# Revit family: Lüftungsrohrschelle , M 8, Gummi
name_source: partatom
category: HLS-Bauteile
revit_build: Autodesk Revit 2017 (Build: 20190507_1515(x64)
units: mm (PartAtom-declared; Revit-internal decimal feet)

## family parameters
Arbeitsebenenbasiert = Ja
Beim Laden mit Abzugskörper schneiden = Nein
Bemaßung runder Anschluss = Durchmesser verwenden
Gemeinsam genutzt = Ja
Immer vertikal = Nein
Raumberechnungspunkt = Nein
Teiletyp = Normal

## types (21) — shared parameters
Anschluss = M8
Bauart = zweiteilig
Baustoffklasse = B2
DF1 = 25 mm  [stored 0.082021 ft]
DS = 6 mm  [stored 0.019685 ft]
DVS = 8 mm  [stored 0.0262467 ft]
Dämmstärke = 6 mm  [stored 0.019685 ft]
Fabrikat = MEFA
Farbe Schalldämmeinlage = schwarz
Firma = MEFA Befestigungs- und Montagesysteme GmbH
Material = Stahl
Material Schalldämmeinlage = TPE
Materialname = S235
Mengeneinheit = St
Oberflaeche = galvanisch verzinkt
Rohraußendurchmesser Zoll = Zoll
Schalldämmeinlage = Gummi
Verschluss = Mutter / Verschluss-Schraube
Verschluss-Schraube = M8
Vorgabe-Ansicht = 1219 mm
max. Temperaturbeständigkeit = 100 °C
max. zul. Last horizontal = 0.00 kN
max. zul. Last vertikal = 0.00 kN
vpe = 1 St
zero-valued in all types: AB, Stärke Material, max. Rohraußendurchmesser, min. Rohraußendurchmesser

## per-type parameters (varying)
- Lüftungsrohrschelle, M 8, DN  71, Gummi: A=22 mm  [stored 0.0721785 ft]; Achsabstand=120 mm; Anschlußhöhe=22 mm; Artikelnummer=0430711; B=145 mm; Breite=145 mm; D=73 mm  [stored 0.239501 ft]; D0=85 mm  [stored 0.278871 ft]; DF2=35 mm  [stored 0.114829 ft]; EAN=4250928409355; Gewicht=0.21 kg; Gewicht pro Bauteil=0.21 kg; H=103 mm; HGA=14 mm  [stored 0.0459318 ft]; Höhe=103 mm; Kurztext1=Lüftungsschelle Standard 20x2,0; Kurztext2=DN 71 M8 TPE; MB=20 mm  [stored 0.0656168 ft]; MD=2 mm  [stored 0.00656168 ft]; Materialmaße=20x2,0 mm; Nennweite DN Rohr=71 mm  [stored 0.23294 ft]; R=43 mm; RM=45 mm; Rohraußendurchmesser=73 mm  [stored 0.239501 ft]; S=120 mm; max. Höhe=103 mm; max. zul. Last=0.80 kN
- Lüftungsrohrschelle, M 8, DN  80, Gummi: A=22 mm  [stored 0.0721785 ft]; Achsabstand=129 mm; Anschlußhöhe=22 mm; Artikelnummer=0430801; B=154 mm; Breite=154 mm; D=82 mm  [stored 0.269029 ft]; D0=94 mm  [stored 0.308399 ft]; DF2=35 mm  [stored 0.114829 ft]; EAN=4250928409409; Gewicht=0.22 kg; Gewicht pro Bauteil=0.22 kg; H=112 mm; HGA=14 mm  [stored 0.0459318 ft]; Höhe=112 mm; Kurztext1=Lüftungsschelle Standard 20x2,0; Kurztext2=DN 80 M8 TPE; MB=20 mm  [stored 0.0656168 ft]; MD=2 mm  [stored 0.00656168 ft]; Materialmaße=20x2,0 mm; Nennweite DN Rohr=80 mm  [stored 0.262467 ft]; R=47 mm  [stored 0.154199 ft]; RM=49 mm  [stored 0.160761 ft]; Rohraußendurchmesser=82 mm  [stored 0.269029 ft]; S=129 mm; max. Höhe=112 mm; max. zul. Last=0.80 kN
- Lüftungsrohrschelle, M 8, DN  90, Gummi: A=22 mm  [stored 0.0721785 ft]; Achsabstand=139 mm; Anschlußhöhe=22 mm; Artikelnummer=0430901; B=164 mm; Breite=164 mm; D=92 mm  [stored 0.301837 ft]; D0=104 mm; DF2=35 mm  [stored 0.114829 ft]; EAN=4250928409454; Gewicht=0.23 kg; Gewicht pro Bauteil=0.23 kg; H=122 mm; HGA=14 mm  [stored 0.0459318 ft]; Höhe=122 mm; Kurztext1=Lüftungsschelle Standard 20x2,0; Kurztext2=DN 90 M8 TPE; MB=20 mm  [stored 0.0656168 ft]; MD=2 mm  [stored 0.00656168 ft]; Materialmaße=20x2,0 mm; Nennweite DN Rohr=90 mm  [stored 0.295276 ft]; R=52 mm  [stored 0.170604 ft]; RM=54 mm  [stored 0.177165 ft]; Rohraußendurchmesser=92 mm  [stored 0.301837 ft]; S=139 mm; max. Höhe=122 mm; max. zul. Last=0.80 kN
- Lüftungsrohrschelle, M 8, DN 100, Gummi: A=22 mm  [stored 0.0721785 ft]; Achsabstand=150 mm; Anschlußhöhe=22 mm; Artikelnummer=0431001; B=175 mm; Breite=175 mm; D=103 mm; D0=115 mm; DF2=35 mm  [stored 0.114829 ft]; EAN=4250928409508; Gewicht=0.25 kg; Gewicht pro Bauteil=0.25 kg; H=133 mm; HGA=14 mm  [stored 0.0459318 ft]; Höhe=133 mm; Kurztext1=Lüftungsschelle Standard 20x2,0; Kurztext2=DN 100 M8 TPE; MB=20 mm  [stored 0.0656168 ft]; MD=2 mm  [stored 0.00656168 ft]; Materialmaße=20x2,0 mm; Nennweite DN Rohr=100 mm; R=58 mm  [stored 0.190289 ft]; RM=60 mm; Rohraußendurchmesser=103 mm; S=150 mm; max. Höhe=133 mm; max. zul. Last=0.80 kN
- Lüftungsrohrschelle, M 8, DN 112, Gummi: A=22 mm  [stored 0.0721785 ft]; Achsabstand=162 mm; Anschlußhöhe=22 mm; Artikelnummer=0431121; B=187 mm; Breite=187 mm; D=115 mm; D0=127 mm; DF2=35 mm  [stored 0.114829 ft]; EAN=4250928409553; Gewicht=0.26 kg; Gewicht pro Bauteil=0.26 kg; H=145 mm; HGA=14 mm  [stored 0.0459318 ft]; Höhe=145 mm; Kurztext1=Lüftungsschelle Standard 20x2,0; Kurztext2=DN 112 M8 TPE; MB=20 mm  [stored 0.0656168 ft]; MD=2 mm  [stored 0.00656168 ft]; Materialmaße=20x2,0 mm; Nennweite DN Rohr=112 mm; R=64 mm; RM=66 mm; Rohraußendurchmesser=115 mm; S=162 mm; max. Höhe=145 mm; max. zul. Last=0.80 kN
- Lüftungsrohrschelle, M 8, DN 125, Gummi: A=22 mm  [stored 0.0721785 ft]; Achsabstand=175 mm; Anschlußhöhe=22 mm; Artikelnummer=0431251; B=200 mm; Breite=200 mm; D=128 mm; D0=140 mm; DF2=35 mm  [stored 0.114829 ft]; EAN=4250928409607; Gewicht=0.28 kg; Gewicht pro Bauteil=0.28 kg; H=158 mm; HGA=14 mm  [stored 0.0459318 ft]; Höhe=158 mm; Kurztext1=Lüftungsschelle Standard 20x2,0; Kurztext2=DN 125 M8 TPE; MB=20 mm  [stored 0.0656168 ft]; MD=2 mm  [stored 0.00656168 ft]; Materialmaße=20x2,0 mm; Nennweite DN Rohr=125 mm; R=70 mm  [stored 0.229659 ft]; RM=72 mm  [stored 0.23622 ft]; Rohraußendurchmesser=128 mm; S=175 mm; max. Höhe=158 mm; max. zul. Last=0.80 kN
- Lüftungsrohrschelle, M 8, DN 140, Gummi: A=22 mm  [stored 0.0721785 ft]; Achsabstand=190 mm; Anschlußhöhe=22 mm; Artikelnummer=0431401; B=215 mm; Breite=215 mm; D=143 mm; D0=155 mm; DF2=35 mm  [stored 0.114829 ft]; EAN=4250928409652; Gewicht=0.30 kg; Gewicht pro Bauteil=0.30 kg; H=173 mm; HGA=14 mm  [stored 0.0459318 ft]; Höhe=173 mm; Kurztext1=Lüftungsschelle Standard 20x2,0; Kurztext2=DN 140 M8 TPE; MB=20 mm  [stored 0.0656168 ft]; MD=2 mm  [stored 0.00656168 ft]; Materialmaße=20x2,0 mm; Nennweite DN Rohr=140 mm; R=78 mm; RM=80 mm  [stored 0.262467 ft]; Rohraußendurchmesser=143 mm; S=190 mm; max. Höhe=173 mm; max. zul. Last=0.80 kN
- Lüftungsrohrschelle, M 8, DN 150, Gummi: A=22 mm  [stored 0.0721785 ft]; Achsabstand=200 mm; Anschlußhöhe=22 mm; Artikelnummer=0431501; B=225 mm; Breite=225 mm; D=153 mm; D0=165 mm; DF2=35 mm  [stored 0.114829 ft]; EAN=4250928409706; Gewicht=0.32 kg; Gewicht pro Bauteil=0.32 kg; H=183 mm; HGA=14 mm  [stored 0.0459318 ft]; Höhe=183 mm; Kurztext1=Lüftungsschelle Standard 20x2,0; Kurztext2=DN 150 M8 TPE; MB=20 mm  [stored 0.0656168 ft]; MD=2 mm  [stored 0.00656168 ft]; Materialmaße=20x2,0 mm; Nennweite DN Rohr=150 mm; R=83 mm; RM=85 mm  [stored 0.278871 ft]; Rohraußendurchmesser=153 mm; S=200 mm; max. Höhe=183 mm; max. zul. Last=0.80 kN
- Lüftungsrohrschelle, M 8, DN 160, Gummi: A=22 mm  [stored 0.0721785 ft]; Achsabstand=210 mm; Anschlußhöhe=22 mm; Artikelnummer=0431601; B=235 mm; Breite=235 mm; D=163 mm; D0=175 mm; DF2=35 mm  [stored 0.114829 ft]; EAN=4250928409751; Gewicht=0.33 kg; Gewicht pro Bauteil=0.33 kg; H=193 mm; HGA=14 mm  [stored 0.0459318 ft]; Höhe=193 mm; Kurztext1=Lüftungsschelle Standard 20x2,0; Kurztext2=DN 160 M8 TPE; MB=20 mm  [stored 0.0656168 ft]; MD=2 mm  [stored 0.00656168 ft]; Materialmaße=20x2,0 mm; Nennweite DN Rohr=160 mm; R=88 mm; RM=90 mm  [stored 0.295276 ft]; Rohraußendurchmesser=163 mm; S=210 mm; max. Höhe=193 mm; max. zul. Last=0.80 kN
- Lüftungsrohrschelle, M 8, DN 180, Gummi: A=23 mm; Achsabstand=230 mm; Anschlußhöhe=23 mm; Artikelnummer=0431801; B=255 mm; Breite=255 mm; D=183 mm; D0=195 mm; DF2=34 mm; EAN=4250928409805; Gewicht=0.42 kg; Gewicht pro Bauteil=0.42 kg; H=214 mm; HGA=14 mm  [stored 0.0459318 ft]; Höhe=214 mm; Kurztext1=Lüftungsschelle Standard 20x2,5; Kurztext2=DN 180 M8 TPE; MB=20 mm  [stored 0.0656168 ft]; MD=3 mm  [stored 0.00984252 ft]; Materialmaße=20x2,5 mm; Nennweite DN Rohr=180 mm; R=98 mm; RM=100 mm; Rohraußendurchmesser=183 mm; S=230 mm; max. Höhe=214 mm; max. zul. Last=1.50 kN
- Lüftungsrohrschelle, M 8, DN 200, Gummi: A=23 mm; Achsabstand=250 mm; Anschlußhöhe=23 mm; Artikelnummer=0432001; B=275 mm; Breite=275 mm; D=203 mm; D0=215 mm; DF2=34 mm; EAN=4250928409850; Gewicht=0.45 kg; Gewicht pro Bauteil=0.45 kg; H=234 mm; HGA=14 mm  [stored 0.0459318 ft]; Höhe=233 mm; Kurztext1=Lüftungsschelle Standard 20x2,5; Kurztext2=DN 200 M8 TPE; MB=20 mm  [stored 0.0656168 ft]; MD=3 mm  [stored 0.00984252 ft]; Materialmaße=20x2,5 mm; Nennweite DN Rohr=200 mm; R=108 mm; RM=110 mm; Rohraußendurchmesser=203 mm; S=250 mm; max. Höhe=233 mm; max. zul. Last=1.50 kN
- Lüftungsrohrschelle, M 8, DN 224, Gummi: A=23 mm; Achsabstand=274 mm; Anschlußhöhe=23 mm; Artikelnummer=0432241; B=299 mm; Breite=299 mm; D=227 mm; D0=239 mm; DF2=34 mm; EAN=4250928409911; Gewicht=0.49 kg; Gewicht pro Bauteil=0.49 kg; H=258 mm; HGA=14 mm  [stored 0.0459318 ft]; Höhe=258 mm; Kurztext1=Lüftungsschelle Standard 20x2,5; Kurztext2=DN 224 M8 TPE; MB=20 mm  [stored 0.0656168 ft]; MD=3 mm  [stored 0.00984252 ft]; Materialmaße=20x2,5 mm; Nennweite DN Rohr=224 mm; R=120 mm; RM=122 mm; Rohraußendurchmesser=227 mm; S=274 mm; max. Höhe=258 mm; max. zul. Last=1.50 kN
- Lüftungsrohrschelle, M 8, DN 250, Gummi: A=22 mm  [stored 0.0721785 ft]; Achsabstand=300 mm; Anschlußhöhe=23 mm; Artikelnummer=0432501; B=325 mm; Breite=325 mm; D=253 mm; D0=265 mm; DF2=34 mm; EAN=4250928409973; Gewicht=0.54 kg; Gewicht pro Bauteil=0.54 kg; H=283 mm; HGA=13 mm; Höhe=283 mm; Kurztext1=Lüftungsschelle Standard 20x2,5; Kurztext2=DN 250 M8 TPE; MB=20 mm  [stored 0.0656168 ft]; MD=3 mm  [stored 0.00984252 ft]; Materialmaße=20x2,5 mm; Nennweite DN Rohr=250 mm; R=133 mm; RM=135 mm; Rohraußendurchmesser=253 mm; S=300 mm; max. Höhe=283 mm; max. zul. Last=1.50 kN
- Lüftungsrohrschelle, M 8, DN 280, Gummi: A=24 mm  [stored 0.0787402 ft]; Achsabstand=332 mm; Anschlußhöhe=23 mm; Artikelnummer=0432801; B=357 mm; Breite=357 mm; D=283 mm; D0=295 mm; DF2=36 mm  [stored 0.11811 ft]; EAN=4250928410030; Gewicht=0.71 kg; Gewicht pro Bauteil=0.71 kg; H=315 mm; HGA=15 mm  [stored 0.0492126 ft]; Höhe=315 mm; Kurztext1=Lüftungsschelle Standard 25x2,5; Kurztext2=DN 280 M8 TPE; MB=25 mm  [stored 0.082021 ft]; MD=3 mm  [stored 0.00984252 ft]; Materialmaße=25x2,5 mm; Nennweite DN Rohr=280 mm; R=148 mm; RM=150 mm; Rohraußendurchmesser=283 mm; S=332 mm; max. Höhe=315 mm; max. zul. Last=2.00 kN
- Lüftungsrohrschelle, M 8, DN 300, Gummi: A=25 mm  [stored 0.082021 ft]; Achsabstand=353 mm; Anschlußhöhe=23 mm; Artikelnummer=0433001; B=378 mm; Breite=378 mm; D=304 mm; D0=316 mm; DF2=36 mm  [stored 0.11811 ft]; EAN=4250928410092; Gewicht=0.75 kg; Gewicht pro Bauteil=0.75 kg; H=337 mm; HGA=16 mm  [stored 0.0524934 ft]; Höhe=337 mm; Kurztext1=Lüftungsschelle Standard 25x2,5; Kurztext2=DN 300 M8 TPE; MB=25 mm  [stored 0.082021 ft]; MD=3 mm  [stored 0.00984252 ft]; Materialmaße=25x2,5 mm; Nennweite DN Rohr=300 mm; R=158 mm; RM=161 mm; Rohraußendurchmesser=304 mm; S=353 mm; max. Höhe=337 mm; max. zul. Last=2.00 kN
- Lüftungsrohrschelle, M 8, DN 315, Gummi: A=25 mm  [stored 0.082021 ft]; Achsabstand=368 mm; Anschlußhöhe=23 mm; Artikelnummer=0433151; B=393 mm; Breite=393 mm; D=319 mm; D0=331 mm; DF2=36 mm  [stored 0.11811 ft]; EAN=4250928410153; Gewicht=0.78 kg; Gewicht pro Bauteil=0.78 kg; H=352 mm; HGA=16 mm  [stored 0.0524934 ft]; Höhe=352 mm; Kurztext1=Lüftungsschelle Standard 25x2,5; Kurztext2=DN 315 M8 TPE; MB=25 mm  [stored 0.082021 ft]; MD=3 mm  [stored 0.00984252 ft]; Materialmaße=25x2,5 mm; Nennweite DN Rohr=315 mm; R=166 mm; RM=168 mm; Rohraußendurchmesser=319 mm; S=368 mm; max. Höhe=352 mm; max. zul. Last=2.00 kN
- Lüftungsrohrschelle, M 8, DN 355, Gummi: A=25 mm  [stored 0.082021 ft]; Achsabstand=408 mm; Anschlußhöhe=23 mm; Artikelnummer=0433551; B=433 mm; Breite=433 mm; D=359 mm; D0=371 mm; DF2=36 mm  [stored 0.11811 ft]; EAN=4250928410214; Gewicht=0.87 kg; Gewicht pro Bauteil=0.87 kg; H=392 mm; HGA=16 mm  [stored 0.0524934 ft]; Höhe=392 mm; Kurztext1=Lüftungsschelle Standard 25x2,5; Kurztext2=DN 355 M8 TPE; MB=25 mm  [stored 0.082021 ft]; MD=3 mm  [stored 0.00984252 ft]; Materialmaße=25x2,5 mm; Nennweite DN Rohr=355 mm; R=186 mm; RM=188 mm; Rohraußendurchmesser=359 mm; S=408 mm; max. Höhe=392 mm; max. zul. Last=2.00 kN
- Lüftungsrohrschelle, M 8, DN 400, Gummi: A=25 mm  [stored 0.082021 ft]; Achsabstand=453 mm; Anschlußhöhe=23 mm; Artikelnummer=0434001; B=478 mm; Breite=478 mm; D=404 mm; D0=416 mm; DF2=36 mm  [stored 0.11811 ft]; EAN=4250928410276; Gewicht=0.96 kg; Gewicht pro Bauteil=0.96 kg; H=437 mm; HGA=16 mm  [stored 0.0524934 ft]; Höhe=437 mm; Kurztext1=Lüftungsschelle Standard 25x2,5; Kurztext2=DN 400 M8 TPE; MB=25 mm  [stored 0.082021 ft]; MD=3 mm  [stored 0.00984252 ft]; Materialmaße=25x2,5 mm; Nennweite DN Rohr=400 mm; R=208 mm; RM=211 mm; Rohraußendurchmesser=404 mm; S=453 mm; max. Höhe=437 mm; max. zul. Last=2.00 kN
- Lüftungsrohrschelle, M 8, DN 450, Gummi: A=25 mm  [stored 0.082021 ft]; Achsabstand=503 mm; Anschlußhöhe=23 mm; Artikelnummer=0434501; B=528 mm; Breite=528 mm; D=454 mm; D0=466 mm; DF2=36 mm  [stored 0.11811 ft]; EAN=4250928410337; Gewicht=1.07 kg; Gewicht pro Bauteil=1.07 kg; H=487 mm; HGA=16 mm  [stored 0.0524934 ft]; Höhe=487 mm; Kurztext1=Lüftungsschelle Standard 25x2,5; Kurztext2=DN 450 M8 TPE; MB=25 mm  [stored 0.082021 ft]; MD=3 mm  [stored 0.00984252 ft]; Materialmaße=25x2,5 mm; Nennweite DN Rohr=450 mm; R=233 mm; RM=236 mm; Rohraußendurchmesser=454 mm; S=503 mm; max. Höhe=487 mm; max. zul. Last=2.00 kN
- Lüftungsrohrschelle, M 8, DN 500, Gummi: A=25 mm  [stored 0.082021 ft]; Achsabstand=553 mm; Anschlußhöhe=23 mm; Artikelnummer=0435001; B=578 mm; Breite=578 mm; D=504 mm; D0=516 mm; DF2=36 mm  [stored 0.11811 ft]; EAN=4250928410399; Gewicht=1.17 kg; Gewicht pro Bauteil=1.17 kg; H=537 mm; HGA=16 mm  [stored 0.0524934 ft]; Höhe=537 mm; Kurztext1=Lüftungsschelle Standard 25x2,5; Kurztext2=DN 500 M8 TPE; MB=25 mm  [stored 0.082021 ft]; MD=3 mm  [stored 0.00984252 ft]; Materialmaße=25x2,5 mm; Nennweite DN Rohr=500 mm; R=258 mm; RM=261 mm; Rohraußendurchmesser=504 mm; S=553 mm; max. Höhe=537 mm; max. zul. Last=2.00 kN
- Lüftungsrohrschelle, M 8, DN 560, Gummi: A=25 mm  [stored 0.082021 ft]; Achsabstand=613 mm; Anschlußhöhe=23 mm; Artikelnummer=0435601; B=638 mm; Breite=638 mm; D=564 mm; D0=576 mm; DF2=36 mm  [stored 0.11811 ft]; EAN=4250928410450; Gewicht=1.29 kg; Gewicht pro Bauteil=1.29 kg; H=597 mm; HGA=16 mm  [stored 0.0524934 ft]; Höhe=597 mm; Kurztext1=Lüftungsschelle Standard 25x2,5; Kurztext2=DN 560 M8 TPE; MB=25 mm  [stored 0.082021 ft]; MD=3 mm  [stored 0.00984252 ft]; Materialmaße=25x2,5 mm; Nennweite DN Rohr=560 mm; R=288 mm; RM=291 mm; Rohraußendurchmesser=564 mm; S=613 mm; max. Höhe=597 mm; max. zul. Last=2.00 kN

note: [stored X ft] marks values corroborated as IEEE doubles in the binary element streams (Revit-internal decimal feet)

## geometry (parser evidence)
native form markers: Sweep x6
no freeform markers — native parametric forms only
